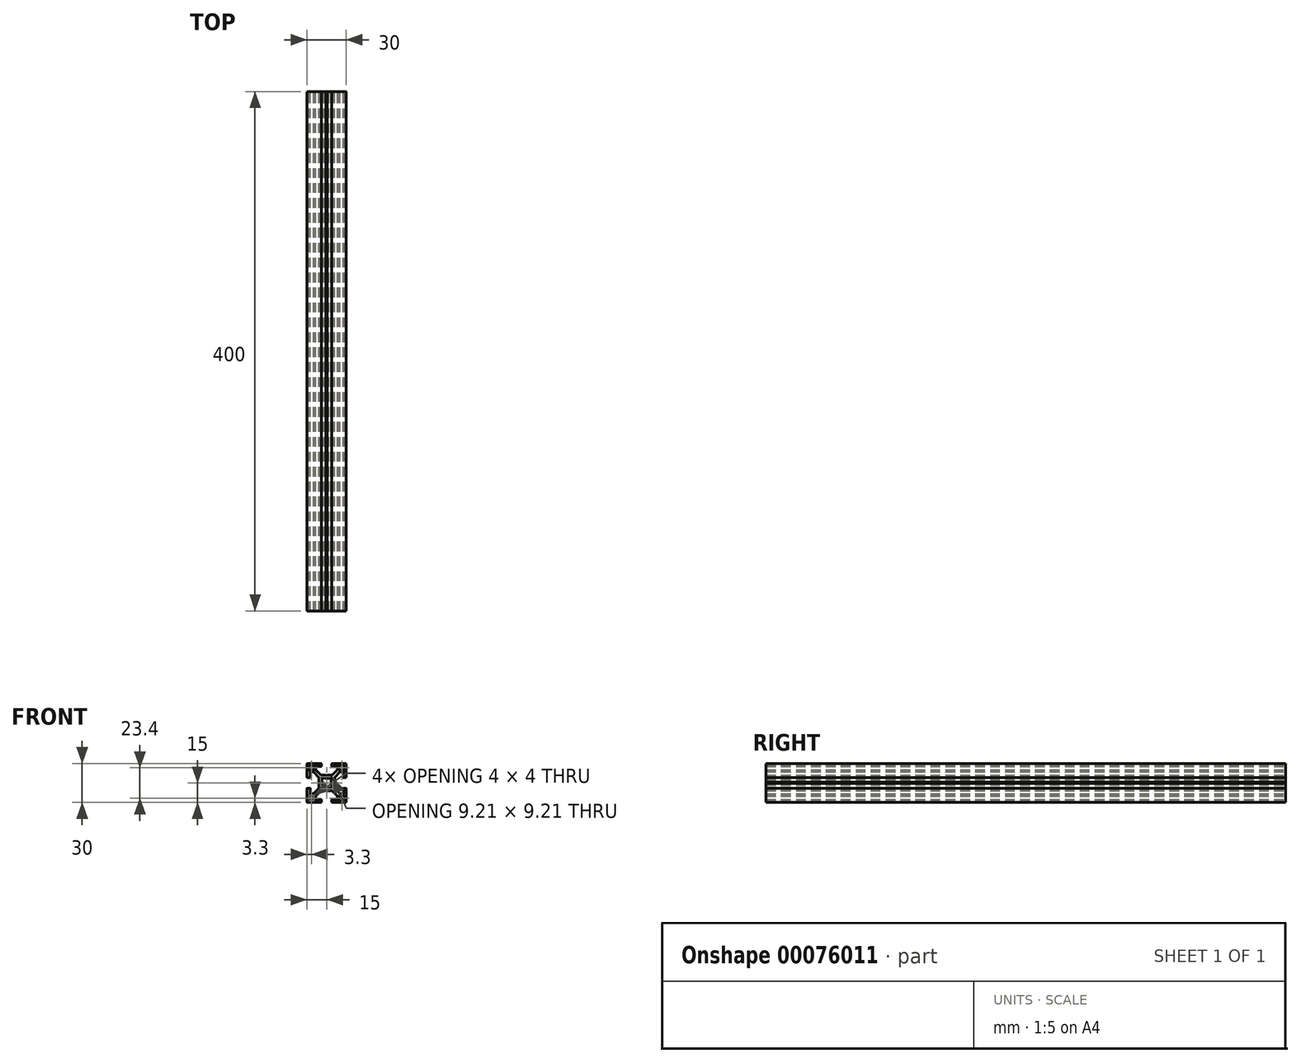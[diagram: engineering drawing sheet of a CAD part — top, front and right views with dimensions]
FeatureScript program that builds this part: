
annotation { "Feature Type Name" : "Feature", "Feature Type Description" : "" }
export const myFeature = defineFeature(function(context is Context, id is Id, definition is map)
    precondition{}
    {
        {
            var Q0;
            Q0=qCreatedBy(makeId("Front.planeOp"),FACE);
            var sketch = newSketch(context, id + "F0", { "sketchPlane" : qUnion([Q0])});
            skPoint(sketch, "E0.middle", {"position": v(0, 0) * mm});
            skLineSegment(sketch, "E1.bottom", {"start": v(-13.7, 13.7) * mm, "end": v(-9.7, 13.7) * mm});
            skLineSegment(sketch, "E1.top", {"start": v(-13.7, 9.7) * mm, "end": v(-9.7, 9.7) * mm});
            skLineSegment(sketch, "E1.left", {"start": v(-13.7, 13.7) * mm, "end": v(-13.7, 9.7) * mm});
            skLineSegment(sketch, "E1.right", {"start": v(-9.7, 13.7) * mm, "end": v(-9.7, 9.7) * mm});
            skLineSegment(sketch, "E2", {"start": v(-4, 15) * mm, "end": v(-4, 12.7) * mm});
            skLineSegment(sketch, "E3", {"start": v(-4, 12.7) * mm, "end": v(-8.4, 12.7) * mm});
            skPoint(sketch, "E4.endSnap0", {"position": v(-6.2, 12.7) * mm});
            skLineSegment(sketch, "E5", {"start": v(8.4, 12.7) * mm, "end": v(4, 12.7) * mm});
            skLineSegment(sketch, "E6", {"start": v(4, 12.7) * mm, "end": v(4, 15) * mm});
            skLineSegment(sketch, "E7.MirrorCS", {"start": v(9.7, 13.7) * mm, "end": v(9.7, 9.7) * mm});
            skLineSegment(sketch, "E8.MirrorCS", {"start": v(13.7, 13.7) * mm, "end": v(9.7, 13.7) * mm});
            skLineSegment(sketch, "E9.MirrorCS", {"start": v(13.7, 13.7) * mm, "end": v(13.7, 9.7) * mm});
            skLineSegment(sketch, "E10.MirrorCS", {"start": v(13.7, 9.7) * mm, "end": v(9.7, 9.7) * mm});
            skLineSegment(sketch, "E11", {"start": v(4, 15) * mm, "end": v(4, 12.7) * mm});
            skLineSegment(sketch, "E12", {"start": v(-8.4, 12.7) * mm, "end": v(-8.4, 10.13) * mm});
            skLineSegment(sketch, "E13.MirrorCS", {"start": v(8.4, 12.7) * mm, "end": v(8.4, 10.13) * mm});
            skLineSegment(sketch, "E14", {"start": v(-15, 4) * mm, "end": v(-12.7, 4) * mm});
            skLineSegment(sketch, "E15", {"start": v(-12.7, 4) * mm, "end": v(-12.7, 8.4) * mm});
            skLineSegment(sketch, "E16", {"start": v(-12.7, 8.4) * mm, "end": v(-10.2, 8.4) * mm});
            skLineSegment(sketch, "E17.MirrorCS", {"start": v(-15, -4) * mm, "end": v(-12.7, -4) * mm});
            skLineSegment(sketch, "E18.MirrorCS", {"start": v(-12.7, -8.4) * mm, "end": v(-10.2, -8.4) * mm});
            skLineSegment(sketch, "E19.MirrorCS", {"start": v(-12.7, -4) * mm, "end": v(-12.7, -8.4) * mm});
            skLineSegment(sketch, "E20", {"start": v(-4.6, 3.19) * mm, "end": v(-3.19, 4.6) * mm});
            skLineSegment(sketch, "E21", {"start": v(-4.6, 3.19) * mm, "end": v(-3.9, 3.9) * mm});
            skLineSegment(sketch, "E22", {"start": v(-3.9, 3.9) * mm, "end": v(-3.19, 4.6) * mm});
            skLineSegment(sketch, "E23", {"start": v(-3.9, 3.9) * mm, "end": v(-4.6, 3.19) * mm});
            skLineSegment(sketch, "E24", {"start": v(-4.6, 3.19) * mm, "end": v(-3.19, 1.78) * mm});
            skLineSegment(sketch, "E25", {"start": v(-3.19, 4.6) * mm, "end": v(-1.78, 3.19) * mm});
            skLineSegment(sketch, "E26.MirrorCS", {"start": v(3.19, -4.6) * mm, "end": v(1.78, -3.19) * mm});
            skLineSegment(sketch, "E27.MirrorCS", {"start": v(3.19, -4.6) * mm, "end": v(3.9, -3.9) * mm});
            skLineSegment(sketch, "E28.MirrorCS", {"start": v(3.19, -4.6) * mm, "end": v(4.6, -3.19) * mm});
            skLineSegment(sketch, "E29.MirrorCS", {"start": v(4.6, -3.19) * mm, "end": v(3.19, -1.78) * mm});
            skLineSegment(sketch, "E30", {"start": v(1.78, 3.19) * mm, "end": v(3.19, 4.6) * mm});
            skLineSegment(sketch, "E31", {"start": v(3.19, 4.6) * mm, "end": v(3.9, 3.9) * mm});
            skLineSegment(sketch, "E32", {"start": v(3.9, 3.9) * mm, "end": v(4.6, 3.19) * mm});
            skLineSegment(sketch, "E33", {"start": v(4.6, 3.19) * mm, "end": v(3.19, 1.78) * mm});
            skLineSegment(sketch, "E34.MirrorCS", {"start": v(-3.19, -1.78) * mm, "end": v(-4.6, -3.19) * mm});
            skLineSegment(sketch, "E35.MirrorCS", {"start": v(-4.6, -3.19) * mm, "end": v(-3.9, -3.9) * mm});
            skLineSegment(sketch, "E36.MirrorCS", {"start": v(-3.9, -3.9) * mm, "end": v(-3.19, -4.6) * mm});
            skLineSegment(sketch, "E37.MirrorCS", {"start": v(-3.19, -4.6) * mm, "end": v(-1.78, -3.19) * mm});
            skArc(sketch, "E38", {"start": v(1.78, 3.19) * mm, "mid": v(0, 3.65) * mm, "end": v(-1.78, 3.19) * mm});
            skArc(sketch, "E39", {"start": v(3.19, -1.78) * mm, "mid": v(3.65, 0) * mm, "end": v(3.19, 1.78) * mm});
            skArc(sketch, "E40", {"start": v(-1.78, -3.19) * mm, "mid": v(0, -3.65) * mm, "end": v(1.78, -3.19) * mm});
            skArc(sketch, "E41", {"start": v(-3.19, 1.78) * mm, "mid": v(-3.64, 0) * mm, "end": v(-3.19, -1.78) * mm});
            skLineSegment(sketch, "E42", {"start": v(-10.2, 8.4) * mm, "end": v(-6, 4.2) * mm});
            skLineSegment(sketch, "E43", {"start": v(-8.4, 10.13) * mm, "end": v(-4.27, 6) * mm});
            skLineSegment(sketch, "E44.MirrorCS", {"start": v(8.4, 10.13) * mm, "end": v(4.27, 6) * mm});
            skLineSegment(sketch, "E45.MirrorCS", {"start": v(10.2, 8.4) * mm, "end": v(6, 4.2) * mm});
            skLineSegment(sketch, "E46.MirrorCS", {"start": v(-10.2, -8.4) * mm, "end": v(-6, -4.2) * mm});
            skLineSegment(sketch, "E47.MirrorCS", {"start": v(-4, -15) * mm, "end": v(-4, -12.7) * mm});
            skLineSegment(sketch, "E48.MirrorCS", {"start": v(-4, -12.7) * mm, "end": v(-8.4, -12.7) * mm});
            skLineSegment(sketch, "E49.MirrorCS", {"start": v(-8.4, -12.7) * mm, "end": v(-8.4, -10.13) * mm});
            skLineSegment(sketch, "E50.MirrorCS", {"start": v(-8.4, -10.13) * mm, "end": v(-4.27, -6) * mm});
            skLineSegment(sketch, "E51.MirrorCS", {"start": v(8.4, -10.13) * mm, "end": v(4.27, -6) * mm});
            skLineSegment(sketch, "E52.MirrorCS", {"start": v(8.4, -12.7) * mm, "end": v(8.4, -10.13) * mm});
            skLineSegment(sketch, "E53.MirrorCS", {"start": v(8.4, -12.7) * mm, "end": v(4, -12.7) * mm});
            skLineSegment(sketch, "E54.MirrorCS", {"start": v(4, -12.7) * mm, "end": v(4, -15) * mm});
            skLineSegment(sketch, "E55.MirrorCS", {"start": v(12.7, 8.4) * mm, "end": v(10.2, 8.4) * mm});
            skLineSegment(sketch, "E56.MirrorCS", {"start": v(12.7, 4) * mm, "end": v(12.7, 8.4) * mm});
            skLineSegment(sketch, "E57.MirrorCS", {"start": v(15, 4) * mm, "end": v(12.7, 4) * mm});
            skLineSegment(sketch, "E58.MirrorCS", {"start": v(15, -4) * mm, "end": v(12.7, -4) * mm});
            skLineSegment(sketch, "E59.MirrorCS", {"start": v(12.7, -8.4) * mm, "end": v(10.2, -8.4) * mm});
            skLineSegment(sketch, "E60.MirrorCS", {"start": v(10.2, -8.4) * mm, "end": v(6, -4.2) * mm});
            skLineSegment(sketch, "E61.MirrorCS", {"start": v(12.7, -4) * mm, "end": v(12.7, -8.4) * mm});
            skLineSegment(sketch, "E62.MirrorCS", {"start": v(13.7, -9.7) * mm, "end": v(9.7, -9.7) * mm});
            skLineSegment(sketch, "E63.MirrorCS", {"start": v(9.7, -13.7) * mm, "end": v(9.7, -9.7) * mm});
            skLineSegment(sketch, "E64.MirrorCS", {"start": v(13.7, -13.7) * mm, "end": v(9.7, -13.7) * mm});
            skLineSegment(sketch, "E65.MirrorCS", {"start": v(13.7, -13.7) * mm, "end": v(13.7, -9.7) * mm});
            skLineSegment(sketch, "E66.MirrorCS", {"start": v(-13.7, -9.7) * mm, "end": v(-9.7, -9.7) * mm});
            skLineSegment(sketch, "E67.MirrorCS", {"start": v(-13.7, -13.7) * mm, "end": v(-13.7, -9.7) * mm});
            skLineSegment(sketch, "E68.MirrorCS", {"start": v(-13.7, -13.7) * mm, "end": v(-9.7, -13.7) * mm});
            skLineSegment(sketch, "E69.MirrorCS", {"start": v(-9.7, -13.7) * mm, "end": v(-9.7, -9.7) * mm});
            skLineSegment(sketch, "E70", {"start": v(-15, 4) * mm, "end": v(-15, 15) * mm});
            skLineSegment(sketch, "E71", {"start": v(4, 15) * mm, "end": v(15, 15) * mm});
            skLineSegment(sketch, "E72", {"start": v(15, -4) * mm, "end": v(15, -15) * mm});
            skLineSegment(sketch, "E73", {"start": v(-4, 15) * mm, "end": v(-15, 15) * mm});
            skLineSegment(sketch, "E74", {"start": v(-15, -4) * mm, "end": v(-15, -15) * mm});
            skLineSegment(sketch, "E75", {"start": v(4, -15) * mm, "end": v(15, -15) * mm});
            skLineSegment(sketch, "E76", {"start": v(-4, -15) * mm, "end": v(-15, -15) * mm});
            skLineSegment(sketch, "E77", {"start": v(15, 4) * mm, "end": v(15, 15) * mm});
            skLineSegment(sketch, "E78", {"start": v(-4.27, 6) * mm, "end": v(-0.5, 6) * mm});
            skLineSegment(sketch, "E79", {"start": v(0.5, 6) * mm, "end": v(4.27, 6) * mm});
            skLineSegment(sketch, "E80", {"start": v(0, 5.5) * mm, "end": v(0.5, 6) * mm});
            skLineSegment(sketch, "E81", {"start": v(-0.5, 6) * mm, "end": v(0, 5.5) * mm});
            skLineSegment(sketch, "E82", {"start": v(-0.5, 6) * mm, "end": v(-4.27, 6) * mm});
            skLineSegment(sketch, "E83.MirrorCS", {"start": v(-4.27, -6) * mm, "end": v(-0.5, -6) * mm});
            skLineSegment(sketch, "E84.MirrorCS", {"start": v(-0.5, -6) * mm, "end": v(0, -5.5) * mm});
            skLineSegment(sketch, "E85.MirrorCS", {"start": v(0, -5.5) * mm, "end": v(0.5, -6) * mm});
            skLineSegment(sketch, "E86.MirrorCS", {"start": v(0.5, -6) * mm, "end": v(4.27, -6) * mm});
            skLineSegment(sketch, "E87", {"start": v(-6, 0.5) * mm, "end": v(-5.5, 0) * mm});
            skLineSegment(sketch, "E88", {"start": v(-5.5, 0) * mm, "end": v(-6, -0.5) * mm});
            skLineSegment(sketch, "E89", {"start": v(-6, -4.2) * mm, "end": v(-6, -0.5) * mm});
            skLineSegment(sketch, "E90", {"start": v(-6, 0.5) * mm, "end": v(-6, 4.2) * mm});
            skLineSegment(sketch, "E91.MirrorCS", {"start": v(6, 0.5) * mm, "end": v(6, 4.2) * mm});
            skLineSegment(sketch, "E92.MirrorCS", {"start": v(6, 0.5) * mm, "end": v(5.5, 0) * mm});
            skLineSegment(sketch, "E93.MirrorCS", {"start": v(5.5, 0) * mm, "end": v(6, -0.5) * mm});
            skLineSegment(sketch, "E94.MirrorCS", {"start": v(6, -4.2) * mm, "end": v(6, -0.5) * mm});
            skSolve(sketch);
        }
        {
            var Q0;
            Q0 = qSketchRegion(id + "F0", true);
            extrude(context, id + "F1", {"entities" : qUnion([Q0]), "depth" : 400 * mm});
        }
        {
            var Q0;
            Q0=makeQuery(id+"F1.opExtrude","SWEPT_EDGE",EDGE,{"disambiguationData":[OSD([sQuery(id+"F0.wireOp",EDGE,"E2"),sQuery(id+"F0.wireOp",EDGE,"E73")])]});
            var Q1;
            Q1=makeQuery(id+"F1.opExtrude","SWEPT_EDGE",EDGE,{"disambiguationData":[OSD([sQuery(id+"F0.wireOp",EDGE,"E11"),sQuery(id+"F0.wireOp",EDGE,"E71")])]});
            var Q2;
            Q2=makeQuery(id+"F1.opExtrude","SWEPT_EDGE",EDGE,{"disambiguationData":[OSD([sQuery(id+"F0.wireOp",EDGE,"E70"),sQuery(id+"F0.wireOp",EDGE,"E73")])]});
            var Q3;
            Q3=makeQuery(id+"F1.opExtrude","SWEPT_EDGE",EDGE,{"disambiguationData":[OSD([sQuery(id+"F0.wireOp",EDGE,"E71"),sQuery(id+"F0.wireOp",EDGE,"E77")])]});
            var Q4;
            Q4=makeQuery(id+"F1.opExtrude","SWEPT_EDGE",EDGE,{"disambiguationData":[OSD([sQuery(id+"F0.wireOp",EDGE,"E14"),sQuery(id+"F0.wireOp",EDGE,"E15")])]});
            var Q5;
            Q5=makeQuery(id+"F1.opExtrude","SWEPT_EDGE",EDGE,{"disambiguationData":[OSD([sQuery(id+"F0.wireOp",EDGE,"E14"),sQuery(id+"F0.wireOp",EDGE,"E70")])]});
            var Q6;
            Q6=makeQuery(id+"F1.opExtrude","SWEPT_EDGE",EDGE,{"disambiguationData":[OSD([sQuery(id+"F0.wireOp",EDGE,"E17.MirrorCS"),sQuery(id+"F0.wireOp",EDGE,"E74")])]});
            var Q7;
            Q7=makeQuery(id+"F1.opExtrude","SWEPT_EDGE",EDGE,{"disambiguationData":[OSD([sQuery(id+"F0.wireOp",EDGE,"E74"),sQuery(id+"F0.wireOp",EDGE,"E76")])]});
            var Q8;
            Q8=makeQuery(id+"F1.opExtrude","SWEPT_EDGE",EDGE,{"disambiguationData":[OSD([sQuery(id+"F0.wireOp",EDGE,"E47.MirrorCS"),sQuery(id+"F0.wireOp",EDGE,"E76")])]});
            var Q9;
            Q9=makeQuery(id+"F1.opExtrude","SWEPT_EDGE",EDGE,{"disambiguationData":[OSD([sQuery(id+"F0.wireOp",EDGE,"E47.MirrorCS"),sQuery(id+"F0.wireOp",EDGE,"E48.MirrorCS")])]});
            var Q10;
            Q10=makeQuery(id+"F1.opExtrude","SWEPT_EDGE",EDGE,{"disambiguationData":[OSD([sQuery(id+"F0.wireOp",EDGE,"E17.MirrorCS"),sQuery(id+"F0.wireOp",EDGE,"E19.MirrorCS")])]});
            var Q11;
            Q11=makeQuery(id+"F1.opExtrude","SWEPT_EDGE",EDGE,{"disambiguationData":[OSD([sQuery(id+"F0.wireOp",EDGE,"E54.MirrorCS"),sQuery(id+"F0.wireOp",EDGE,"E75")])]});
            var Q12;
            Q12=makeQuery(id+"F1.opExtrude","SWEPT_EDGE",EDGE,{"disambiguationData":[OSD([sQuery(id+"F0.wireOp",EDGE,"E72"),sQuery(id+"F0.wireOp",EDGE,"E75")])]});
            var Q13;
            Q13=makeQuery(id+"F1.opExtrude","SWEPT_EDGE",EDGE,{"disambiguationData":[OSD([sQuery(id+"F0.wireOp",EDGE,"E58.MirrorCS"),sQuery(id+"F0.wireOp",EDGE,"E61.MirrorCS")])]});
            var Q14;
            Q14=makeQuery(id+"F1.opExtrude","SWEPT_EDGE",EDGE,{"disambiguationData":[OSD([sQuery(id+"F0.wireOp",EDGE,"E56.MirrorCS"),sQuery(id+"F0.wireOp",EDGE,"E57.MirrorCS")])]});
            var Q15;
            Q15=makeQuery(id+"F1.opExtrude","SWEPT_EDGE",EDGE,{"disambiguationData":[OSD([sQuery(id+"F0.wireOp",EDGE,"E58.MirrorCS"),sQuery(id+"F0.wireOp",EDGE,"E72")])]});
            var Q16;
            Q16=makeQuery(id+"F1.opExtrude","SWEPT_EDGE",EDGE,{"disambiguationData":[OSD([sQuery(id+"F0.wireOp",EDGE,"E57.MirrorCS"),sQuery(id+"F0.wireOp",EDGE,"E77")])]});
            var Q17;
            Q17=makeQuery(id+"F1.opExtrude","SWEPT_EDGE",EDGE,{"disambiguationData":[OSD([sQuery(id+"F0.wireOp",EDGE,"E3"),sQuery(id+"F0.wireOp",EDGE,"E2")])]});
            var Q18;
            Q18=makeQuery(id+"F1.opExtrude","SWEPT_EDGE",EDGE,{"disambiguationData":[OSD([sQuery(id+"F0.wireOp",EDGE,"E53.MirrorCS"),sQuery(id+"F0.wireOp",EDGE,"E54.MirrorCS")])]});
            var Q19;
            Q19=makeQuery(id+"F1.opExtrude","SWEPT_EDGE",EDGE,{"disambiguationData":[OSD([sQuery(id+"F0.wireOp",EDGE,"E5"),sQuery(id+"F0.wireOp",EDGE,"E11")])]});
            var Q20;
            Q20=makeQuery(id+"F1.opExtrude","SWEPT_EDGE",EDGE,{"disambiguationData":[OSD([sQuery(id+"F0.wireOp",EDGE,"E7.MirrorCS"),sQuery(id+"F0.wireOp",EDGE,"E8.MirrorCS")])]});
            var Q21;
            Q21=makeQuery(id+"F1.opExtrude","SWEPT_EDGE",EDGE,{"disambiguationData":[OSD([sQuery(id+"F0.wireOp",EDGE,"E1.bottom"),sQuery(id+"F0.wireOp",EDGE,"E1.left")])]});
            var Q22;
            Q22=makeQuery(id+"F1.opExtrude","SWEPT_EDGE",EDGE,{"disambiguationData":[OSD([sQuery(id+"F0.wireOp",EDGE,"E66.MirrorCS"),sQuery(id+"F0.wireOp",EDGE,"E67.MirrorCS")])]});
            var Q23;
            Q23=makeQuery(id+"F1.opExtrude","SWEPT_EDGE",EDGE,{"disambiguationData":[OSD([sQuery(id+"F0.wireOp",EDGE,"E62.MirrorCS"),sQuery(id+"F0.wireOp",EDGE,"E63.MirrorCS")])]});
            var Q24;
            Q24=makeQuery(id+"F1.opExtrude","SWEPT_EDGE",EDGE,{"disambiguationData":[OSD([sQuery(id+"F0.wireOp",EDGE,"E1.top"),sQuery(id+"F0.wireOp",EDGE,"E1.right")])]});
            var Q25;
            Q25=makeQuery(id+"F1.opExtrude","SWEPT_EDGE",EDGE,{"disambiguationData":[OSD([sQuery(id+"F0.wireOp",EDGE,"E68.MirrorCS"),sQuery(id+"F0.wireOp",EDGE,"E69.MirrorCS")])]});
            var Q26;
            Q26=makeQuery(id+"F1.opExtrude","SWEPT_EDGE",EDGE,{"disambiguationData":[OSD([sQuery(id+"F0.wireOp",EDGE,"E64.MirrorCS"),sQuery(id+"F0.wireOp",EDGE,"E65.MirrorCS")])]});
            var Q27;
            Q27=makeQuery(id+"F1.opExtrude","SWEPT_EDGE",EDGE,{"disambiguationData":[OSD([sQuery(id+"F0.wireOp",EDGE,"E9.MirrorCS"),sQuery(id+"F0.wireOp",EDGE,"E10.MirrorCS")])]});
            var Q28;
            Q28=makeQuery(id+"F1.opExtrude","SWEPT_EDGE",EDGE,{"disambiguationData":[OSD([sQuery(id+"F0.wireOp",EDGE,"E8.MirrorCS"),sQuery(id+"F0.wireOp",EDGE,"E9.MirrorCS")])]});
            var Q29;
            Q29=makeQuery(id+"F1.opExtrude","SWEPT_EDGE",EDGE,{"disambiguationData":[OSD([sQuery(id+"F0.wireOp",EDGE,"E1.bottom"),sQuery(id+"F0.wireOp",EDGE,"E1.right")])]});
            var Q30;
            Q30=makeQuery(id+"F1.opExtrude","SWEPT_EDGE",EDGE,{"disambiguationData":[OSD([sQuery(id+"F0.wireOp",EDGE,"E66.MirrorCS"),sQuery(id+"F0.wireOp",EDGE,"E69.MirrorCS")])]});
            var Q31;
            Q31=makeQuery(id+"F1.opExtrude","SWEPT_EDGE",EDGE,{"disambiguationData":[OSD([sQuery(id+"F0.wireOp",EDGE,"E62.MirrorCS"),sQuery(id+"F0.wireOp",EDGE,"E65.MirrorCS")])]});
            var Q32;
            Q32=makeQuery(id+"F1.opExtrude","SWEPT_EDGE",EDGE,{"disambiguationData":[OSD([sQuery(id+"F0.wireOp",EDGE,"E7.MirrorCS"),sQuery(id+"F0.wireOp",EDGE,"E10.MirrorCS")])]});
            var Q33;
            Q33=makeQuery(id+"F1.opExtrude","SWEPT_EDGE",EDGE,{"disambiguationData":[OSD([sQuery(id+"F0.wireOp",EDGE,"E1.top"),sQuery(id+"F0.wireOp",EDGE,"E1.left")])]});
            var Q34;
            Q34=makeQuery(id+"F1.opExtrude","SWEPT_EDGE",EDGE,{"disambiguationData":[OSD([sQuery(id+"F0.wireOp",EDGE,"E63.MirrorCS"),sQuery(id+"F0.wireOp",EDGE,"E64.MirrorCS")])]});
            var Q35;
            Q35=makeQuery(id+"F1.opExtrude","SWEPT_EDGE",EDGE,{"disambiguationData":[OSD([sQuery(id+"F0.wireOp",EDGE,"E67.MirrorCS"),sQuery(id+"F0.wireOp",EDGE,"E68.MirrorCS")])]});
            fillet(context, id + "F2", {"entities" : qUnion([Q0, Q1, Q2, Q3, Q4, Q5, Q6, Q7, Q8, Q9, Q10, Q11, Q12, Q13, Q14, Q15, Q16, Q17, Q18, Q19, Q20, Q21, Q22, Q23, Q24, Q25, Q26, Q27, Q28, Q29, Q30, Q31, Q32, Q33, Q34, Q35]), "radius" : 0.2 * mm, "tangentPropagation" : true, "allowEdgeOverflow" : false});
        }
    });
